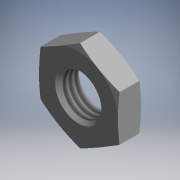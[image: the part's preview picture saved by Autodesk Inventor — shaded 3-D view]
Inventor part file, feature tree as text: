
AUTODESK INVENTOR PART (.ipt)
format: ipt  version: 2017.3 (Build 213256000, 256)  size: 126,976 bytes
history: native  units: mm (DEFAULTED — no unit token found)
features: other x14, sketch x3, revolve x2, extrude x1, thread x1
ambient origin geometry x8: Origin, YZ Plane, XZ Plane, XY Plane, X Axis, Y Axis, Z Axis, Center Point
bodies: Solid1 (feature_tree)
feature tree (21):
  revolve  "Revolution1"  [1 undecoded]
  extrude  "Extrusion1"  Depth=3.647mm TaperAngle=0.0deg
  revolve  "Revolution2"  [1 undecoded]
  thread  "Thread1"  [1 undecoded]
  other  "2CYL_XY"
  other  "2CYL_YZ"
  other  "2CYL_ZX"
  other  "2CYL_X"
  other  "2CYL_Y"
  other  "2CYL_Z"
  other  "2CYL_Center"
  other  "din439b_punkt_XY"
  other  "din439b_punkt_YZ"
  other  "din439b_punkt_ZX"
  other  "din439b_punkt_X"
  other  "din439b_punkt_Y"
  other  "din439b_punkt_Z"
  other  "din439b_punkt_Center"
  sketch  "Sketch_1"  dims[d0=360.0deg d1=12.0mm d2=0.0mm]
  sketch  "Sketch_2"  dims[d3=360.0deg d4=3.647mm d5=0.0mm]
  sketch  "Sketch_3"  dims[d6=0.0mm]
note: 3 required parameter values undecoded (feature->parameter linkage not recoverable at this tier; creation-order binding heuristic only, values carry confidence <= 0.55)